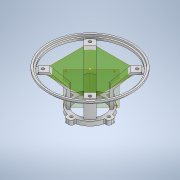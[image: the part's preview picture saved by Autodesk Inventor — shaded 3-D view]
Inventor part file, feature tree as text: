
AUTODESK INVENTOR PART (.ipt)
format: ipt  version: 2020 (Build 240168000, 168)  size: 382,976 bytes
history: native  units: mm
features: other x11, sketch x8, revolve x4, extrude x3, projected_geometry x3, pattern_circular x1
ambient origin geometry x8: Origin, YZ Plane, XZ Plane, XY Plane, X Axis, Y Axis, Z Axis, Center Point
bodies: Body1 (feature_tree)
feature tree (30):
  other  "Твердое тело1"
  extrude  "Выдавливание1"  Depth=34.0mm
  other  "РабПлоскость1"
  other  "РабОсь1"
  revolve  "Вращение1"
  sketch  "Эскиз3"
  other  "РабТочка1"
  extrude  "Выдавливание2"  Depth=45.0mm
  other  "РабТочка2"
  other  "РабТочка3"
  other  "РабТочка4"
  other  "РабПлоскость2"
  sketch  "Эскиз5"
  revolve  "Вращение2"
  revolve  "Вращение3"
  pattern_circular  "Круговой массив1"  Angle=45.0deg  [1 undecoded]
  extrude  "Выдавливание3"  Depth=3.3mm
  revolve  "Вращение4"
  sketch  "Эскиз8"
  sketch  "Эскиз1"
  sketch  "Эскиз2"
  sketch  "Эскиз4"
  projected_geometry  "Спроецированная петля1"
  projected_geometry  "Спроецированная петля2"
  projected_geometry  "Спроецированная петля3"
  other  "РабПлоскость3"
  other  "РабПлоскость4"
  other  "РабПлоскость5"
  sketch  "Эскиз6"
  sketch  "Эскиз7"
note: 1 required parameter value undecoded (feature->parameter linkage not recoverable at this tier; creation-order binding heuristic only, values carry confidence <= 0.55)
